# Revit family: Loading-Equipment_Dock-levellers_Overhead-Door_Edge-dock-leveler
name_source: partatom
category: Specialty Equipment
units: mm (PartAtom-declared; Revit-internal decimal feet)

## family parameters
Classification Number = 23.50.70.14.14
Cut with Voids When Loaded = No
Enable Cutting in Views = No
Host = Face
Maintain Annotation Orientation = No
Part Type = Normal
Room Calculation Point = No
Round Connector Dimension = Use Diameter
Shared = No

## types (3) — shared parameters
Default Elevation = 4' - 0"
Description = The Overhead Door™­ Edge of Dock Leveler provides smooth, safe path for loading docks and trailers.
Main Material = Metal - Overhead Door - Steel
Manufacturer = Overhead Door Corporation
Product Page URL = https://www.overheaddoor.com
Product data url = https://www.bimobject.com
Top Plate Material = Metal - Overhead Door - Steel Checker Plate
URL = https://www.overheaddoor.com

## per-type parameters (varying)
| type | Model | Width |
| E66R | Edge Dock E66R | 5' - 6" |
| E72R | Edge Dock E72R | 6' - 0" |
| E78R | Edge Dock E78R | 6' - 6" |

## geometry (parser evidence)
native form markers: Sweep x9
no freeform markers — native parametric forms only
